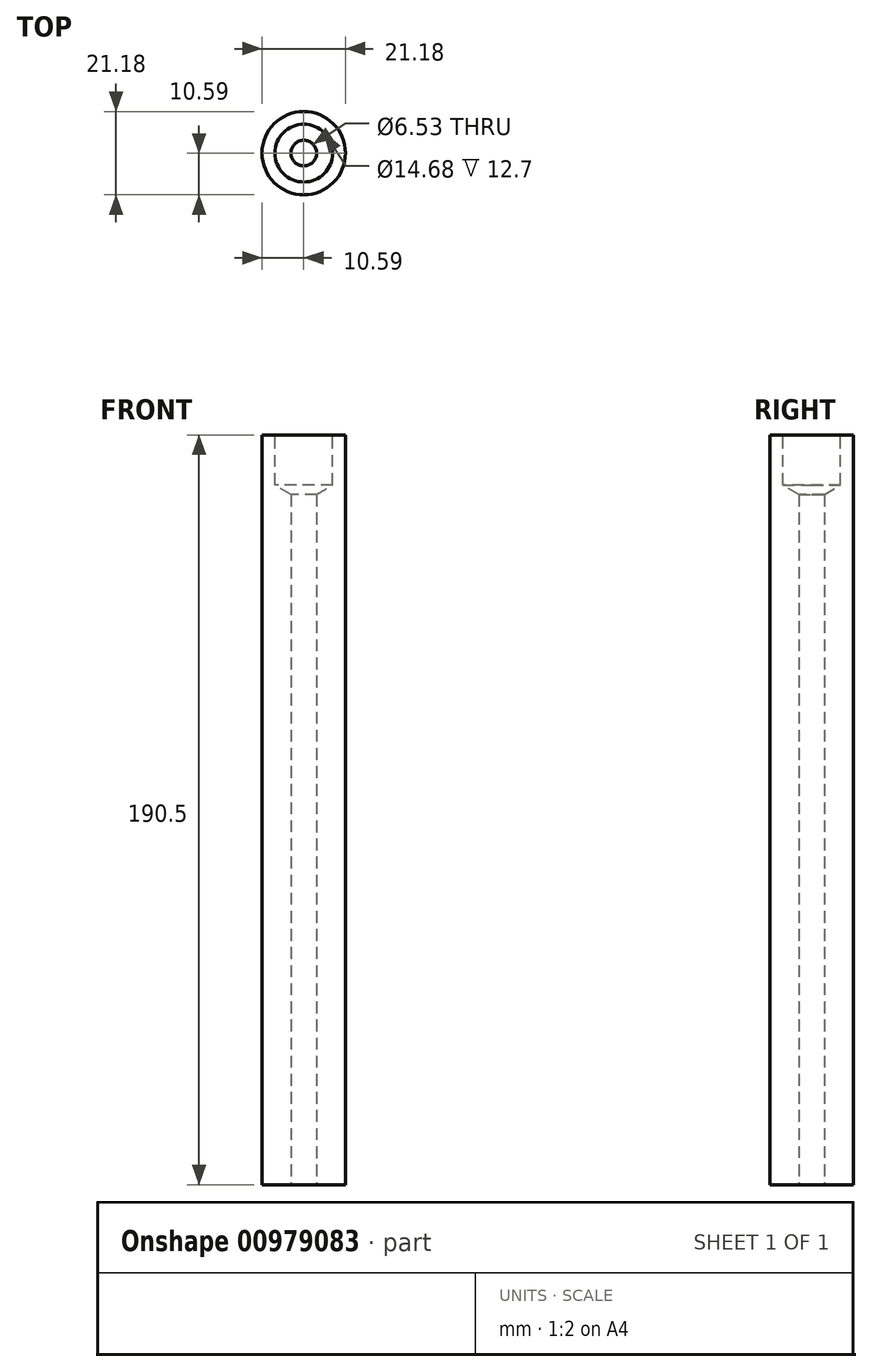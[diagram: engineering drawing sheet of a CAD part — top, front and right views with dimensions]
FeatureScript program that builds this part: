
annotation { "Feature Type Name" : "Feature", "Feature Type Description" : "" }
export const myFeature = defineFeature(function(context is Context, id is Id, definition is map)
    precondition{}
    {
        {
            var Q0;
            Q0=qCreatedBy(makeId("Top.planeOp"),FACE);
            var sketch = newSketch(context, id + "F0", { "sketchPlane" : qUnion([Q0])});
            skCircle(sketch, "E0", {"center": v(0, 0) * mm, "radius": 10.6 * mm});
            skCircle(sketch, "E1", {"center": v(0, 0) * mm, "radius": 3.26 * mm});
            skSolve(sketch);
        }
        {
            var Q0;
            Q0 = qSketchRegion(id + "F0", true);
            extrude(context, id + "F1", {"entities" : qUnion([Q0]), "endBound" : BoundingType.SYMMETRIC, "depth" : 190.5 * mm, "offsetDistance" : 25.4 * mm});
        }
        {
            var Q0;
            Q0=makeQuery(id+"F1.opExtrude","CAP_FACE",FACE,{"disambiguationData":[OSD([sQuery(id+"F0.wireOp",EDGE,"E0"),sQuery(id+"F0.wireOp",EDGE,"E1")])],"isStart":false});
            var sketch = newSketch(context, id + "F2", { "sketchPlane" : qUnion([Q0])});
            skPoint(sketch, "E2", {"position": v(0, 0) * mm});
            skSolve(sketch);
        }
        {
            var Q0;
            Q0=sQuery(id+"F2.wireOp",VERTEX,"E2");
            var Q1;
            Q1=makeQuery(id+"F1.opExtrude","SWEPT_BODY",BODY,{"disambiguationData":[OSD([sQuery(id+"F0.wireOp",EDGE,"E0"),sQuery(id+"F0.wireOp",EDGE,"E1")])]});
            hole(context, id + "F3", {"style" : HoleStyle.SIMPLE, "endStyle" : HoleEndStyle.BLIND, "holeDiameter" : 14.68 * mm, "majorDiameter" : 6.35 * mm, "holeDepth" : 12.7 * mm, "isTappedThrough" : true, "tappedDepth" : 0.5 * mm, "tapClearance" : 3, "locations" : qUnion([Q0]), "scope" : qUnion([Q1])});
        }
    });
